# Revit family: Division_Twelve-Twigz-Dolly-1
name_source: partatom
category: Furniture
units: mm (PartAtom-declared; Revit-internal decimal feet)

## family parameters
Always vertical = Yes
Cut with Voids When Loaded = No
OmniClass Number = 23.40.20.00
OmniClass Title = General Furniture and Specialties
Room Calculation Point = No
Shared = No
Work Plane-Based = No

## types (1)
- 0005
    Assembly Code = E2020200
    Default Elevation = 0"
    Depth = 28 3/4"
    Description = Dolly
    Height = 11 23/32"
    Keynote = 12500
    Low Emitting Finish = Yes
    Low Emitting Material = Yes
    Manufacturer = Division Twelve
    Model = 0005
    Percentage of Recycled Content = 0
    Product Documentation Link = https://division12.com
    Revit Model Built By = https://servex-us.com
    S-1 = Yes
    S-2 = No
    S-3 = No
    Salvage or Reuse = Yes
    Type Comments = Twigz
    URL = https://division12.com
    Width = 23 5/8"

## geometry (parser evidence)
native form markers: Sweep x2
no freeform markers — native parametric forms only
